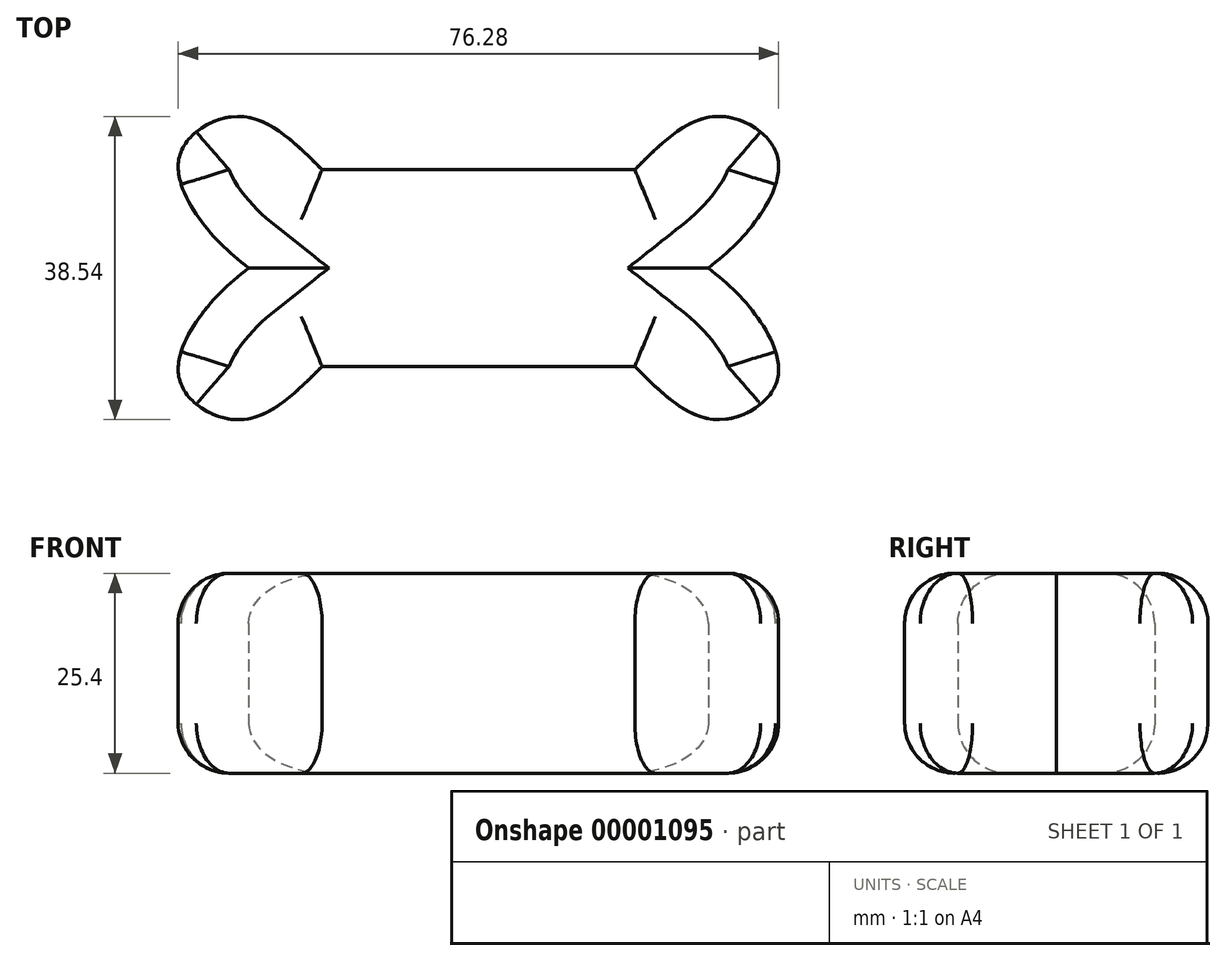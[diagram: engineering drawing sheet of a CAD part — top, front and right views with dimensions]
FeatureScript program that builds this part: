
annotation { "Feature Type Name" : "Feature", "Feature Type Description" : "" }
export const myFeature = defineFeature(function(context is Context, id is Id, definition is map)
    precondition{}
    {
        {
            var Q0;
            Q0=qCreatedBy(makeId("Top.planeOp"),FACE);
            var sketch = newSketch(context, id + "F0", { "sketchPlane" : qUnion([Q0])});
            skFitSpline(sketch, "E0", {"points": [v(-19.86, 12.49) * mm, v(-30.3, 19.26) * mm, v(-37.99, 14.13) * mm, v(-34.14, 4.61) * mm, v(-29.2, 0) * mm], "startDerivative": vector(-34.85, 35.02) * mm, "endDerivative": vector(22.67, -18) * mm});
            skFitSpline(sketch, "E1.0.MirrorCS", {"points": [v(-19.86, -12.49) * mm, v(-30.3, -19.26) * mm, v(-37.99, -14.13) * mm, v(-34.14, -4.61) * mm, v(-29.2, 0) * mm], "startDerivative": vector(-34.85, -35.02) * mm, "endDerivative": vector(22.67, 18) * mm});
            skFitSpline(sketch, "E2.0.MirrorCS", {"points": [v(19.86, 12.49) * mm, v(30.3, 19.26) * mm, v(37.99, 14.13) * mm, v(34.14, 4.61) * mm, v(29.2, 0) * mm], "startDerivative": vector(34.85, 35.02) * mm, "endDerivative": vector(-22.67, -18) * mm});
            skFitSpline(sketch, "E3.0.MirrorCS", {"points": [v(19.86, -12.49) * mm, v(30.3, -19.26) * mm, v(37.99, -14.13) * mm, v(34.14, -4.61) * mm, v(29.2, 0) * mm], "startDerivative": vector(34.85, -35.02) * mm, "endDerivative": vector(-22.67, 18) * mm});
            skLineSegment(sketch, "E4", {"start": v(-19.86, 12.49) * mm, "end": v(19.86, 12.49) * mm});
            skLineSegment(sketch, "E5", {"start": v(-19.86, -12.49) * mm, "end": v(19.86, -12.49) * mm});
            skSolve(sketch);
        }
        {
            var Q0;
            Q0=makeQuery(id+"F0.imprint","IMPRINT",FACE,{"disambiguationData":[TD([[makeQuery(id+"F0.imprint","IMPRINT",EDGE,{"derivedFrom":sQuery(id+"F0.wireOp",EDGE,"E0")}),1.0]])]});
            extrude(context, id + "F1", {"entities" : qUnion([Q0]), "depth" : 25.4 * mm});
        }
        {
            var Q0;
            Q0=makeQuery(id+"F1.opExtrude","CAP_EDGE",EDGE,{"disambiguationData":[OSD([sQuery(id+"F0.wireOp",EDGE,"E1.0.MirrorCS")])],"isStart":false});
            var Q1;
            Q1=makeQuery(id+"F1.opExtrude","CAP_EDGE",EDGE,{"disambiguationData":[OSD([sQuery(id+"F0.wireOp",EDGE,"E0")])],"isStart":false});
            var Q2;
            Q2=makeQuery(id+"F1.opExtrude","CAP_EDGE",EDGE,{"disambiguationData":[OSD([sQuery(id+"F0.wireOp",EDGE,"E4")])],"isStart":false});
            var Q3;
            Q3=makeQuery(id+"F1.opExtrude","CAP_EDGE",EDGE,{"disambiguationData":[OSD([sQuery(id+"F0.wireOp",EDGE,"E2.0.MirrorCS")])],"isStart":false});
            var Q4;
            Q4=makeQuery(id+"F1.opExtrude","CAP_EDGE",EDGE,{"disambiguationData":[OSD([sQuery(id+"F0.wireOp",EDGE,"E3.0.MirrorCS")])],"isStart":false});
            var Q5;
            Q5=makeQuery(id+"F1.opExtrude","CAP_EDGE",EDGE,{"disambiguationData":[OSD([sQuery(id+"F0.wireOp",EDGE,"E5")])],"isStart":true});
            var Q6;
            Q6=makeQuery(id+"F1.opExtrude","CAP_EDGE",EDGE,{"disambiguationData":[OSD([sQuery(id+"F0.wireOp",EDGE,"E1.0.MirrorCS")])],"isStart":true});
            var Q7;
            Q7=makeQuery(id+"F1.opExtrude","CAP_EDGE",EDGE,{"disambiguationData":[OSD([sQuery(id+"F0.wireOp",EDGE,"E3.0.MirrorCS")])],"isStart":true});
            var Q8;
            Q8=makeQuery(id+"F1.opExtrude","CAP_EDGE",EDGE,{"disambiguationData":[OSD([sQuery(id+"F0.wireOp",EDGE,"E2.0.MirrorCS")])],"isStart":true});
            var Q9;
            Q9=makeQuery(id+"F1.opExtrude","CAP_EDGE",EDGE,{"disambiguationData":[OSD([sQuery(id+"F0.wireOp",EDGE,"E0")])],"isStart":true});
            var Q10;
            Q10=makeQuery(id+"F1.opExtrude","CAP_EDGE",EDGE,{"disambiguationData":[OSD([sQuery(id+"F0.wireOp",EDGE,"E4")])],"isStart":true});
            var Q11;
            Q11=makeQuery(id+"F1.opExtrude","CAP_EDGE",EDGE,{"disambiguationData":[OSD([sQuery(id+"F0.wireOp",EDGE,"E5")])],"isStart":false});
            fillet(context, id + "F2", {"entities" : qUnion([Q0, Q1, Q2, Q3, Q4, Q5, Q6, Q7, Q8, Q9, Q10, Q11]), "radius" : 6.35 * mm, "tangentPropagation" : true, "allowEdgeOverflow" : false});
        }
    });
